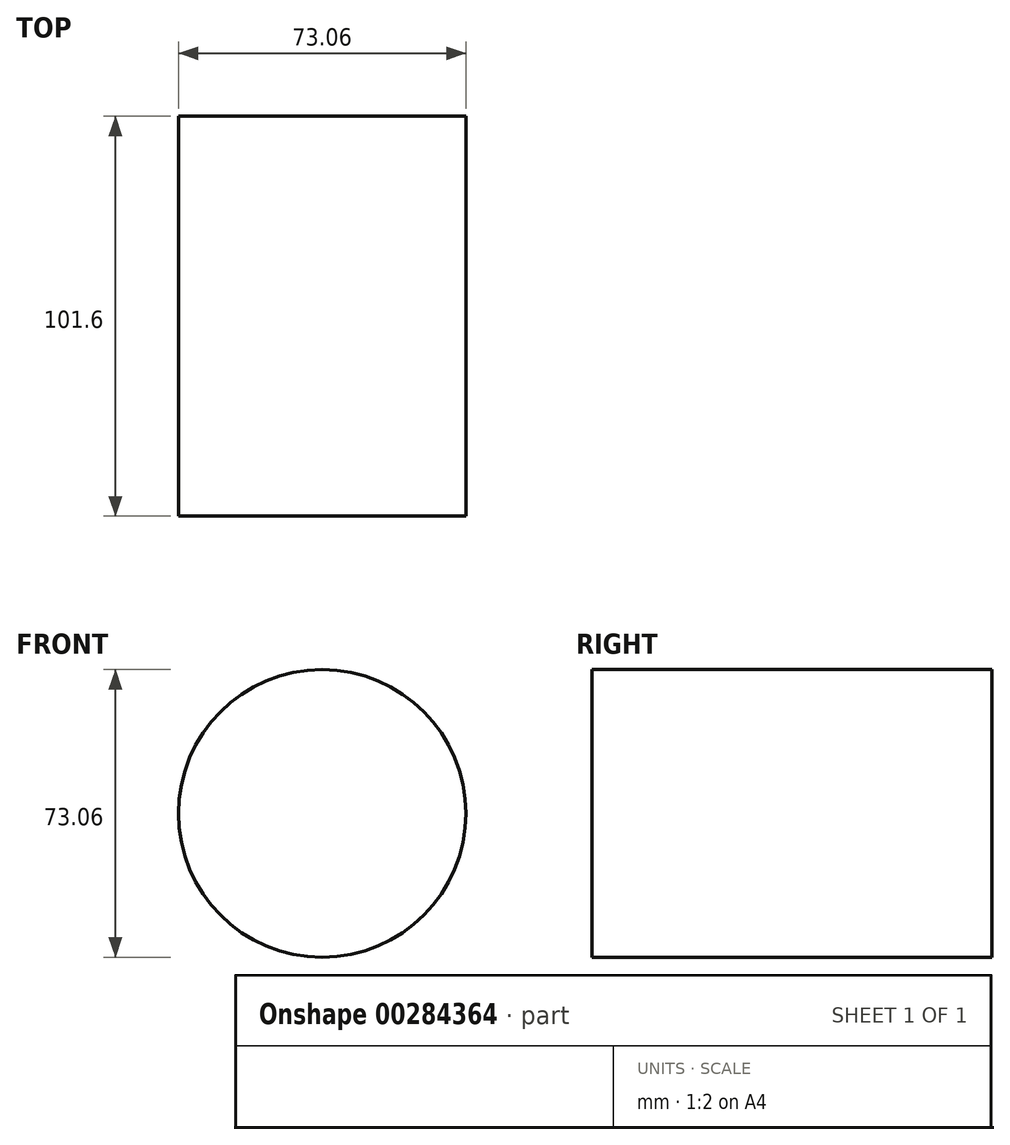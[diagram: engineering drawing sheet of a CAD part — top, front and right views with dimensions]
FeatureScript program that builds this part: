
annotation { "Feature Type Name" : "Feature", "Feature Type Description" : "" }
export const myFeature = defineFeature(function(context is Context, id is Id, definition is map)
    precondition{}
    {
        {
            var Q0;
            Q0=qCreatedBy(makeId("Front.planeOp"),FACE);
            var sketch = newSketch(context, id + "F0", { "sketchPlane" : qUnion([Q0])});
            skCircle(sketch, "E0", {"center": v(0, 0) * mm, "radius": 36.53 * mm});
            skSolve(sketch);
        }
        {
            var Q0;
            Q0 = qSketchRegion(id + "F0", true);
            extrude(context, id + "F1", {"entities" : qUnion([Q0]), "depth" : 101.6 * mm});
        }
    });
